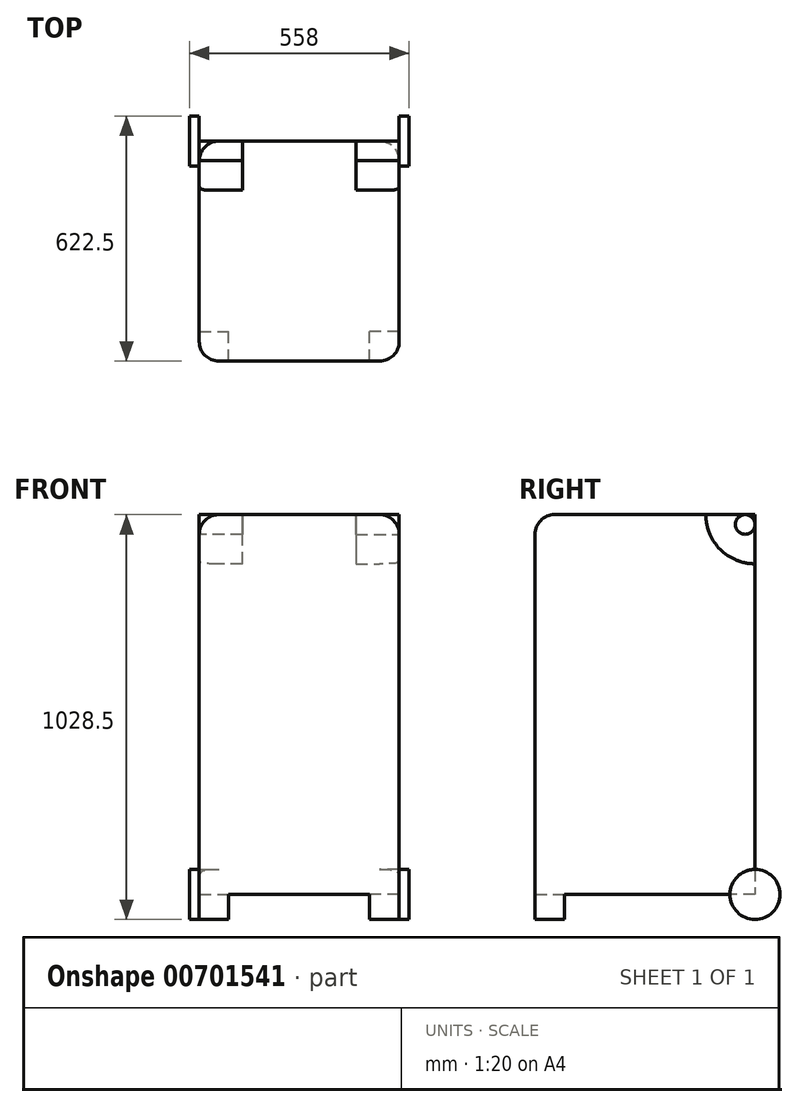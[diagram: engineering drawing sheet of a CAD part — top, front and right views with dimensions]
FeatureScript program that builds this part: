
annotation { "Feature Type Name" : "Feature", "Feature Type Description" : "" }
export const myFeature = defineFeature(function(context is Context, id is Id, definition is map)
    precondition{}
    {
        {
            var Q0;
            Q0=qCreatedBy(makeId("Top.planeOp"),FACE);
            var sketch = newSketch(context, id + "F0", { "sketchPlane" : qUnion([Q0])});
            skLineSegment(sketch, "E0.bottom", {"start": v(-254, 279.5) * mm, "end": v(254, 279.5) * mm});
            skLineSegment(sketch, "E0.top", {"start": v(-254, -279.5) * mm, "end": v(254, -279.5) * mm});
            skLineSegment(sketch, "E0.left", {"start": v(-254, 279.5) * mm, "end": v(-254, -279.5) * mm});
            skLineSegment(sketch, "E0.right", {"start": v(254, 279.5) * mm, "end": v(254, -279.5) * mm});
            skPoint(sketch, "E0.middle", {"position": v(0, 0) * mm});
            skSolve(sketch);
        }
        {
            var Q0;
            Q0=makeQuery(id+"F0.imprint","IMPRINT",FACE,{"disambiguationData":[TD([[makeQuery(id+"F0.imprint","IMPRINT",EDGE,{"derivedFrom":sQuery(id+"F0.wireOp",EDGE,"E0.bottom")}),-1.0]])]});
            extrude(context, id + "F1", {"entities" : qUnion([Q0]), "depth" : 965 * mm, "offsetDistance" : 25 * mm});
        }
        {
            var Q0;
            Q0=makeQuery(id+"F1.opExtrude","SWEPT_FACE",FACE,{"disambiguationData":[OSD([sQuery(id+"F0.wireOp",EDGE,"E0.right")])]});
            var sketch = newSketch(context, id + "F2", { "sketchPlane" : qUnion([Q0])});
            skCircle(sketch, "E1", {"center": v(279.5, 0) * mm, "radius": 63.5 * mm});
            skSolve(sketch);
        }
        {
            var Q0;
            Q0 = qSketchRegion(id + "F2", true);
            extrude(context, id + "F3", {"entities" : qUnion([Q0]), "operationType" : NewBodyOperationType.ADD, "depth" : 25 * mm, "offsetDistance" : 25 * mm});
        }
        {
            var Q0;
            Q0=makeQuery(id+"F1.opExtrude","SWEPT_FACE",FACE,{"disambiguationData":[OSD([sQuery(id+"F0.wireOp",EDGE,"E0.left")])]});
            var sketch = newSketch(context, id + "F4", { "sketchPlane" : qUnion([Q0])});
            skCircle(sketch, "E2", {"center": v(-279.5, 0) * mm, "radius": 63.5 * mm});
            skSolve(sketch);
        }
        {
            var Q0;
            Q0 = qSketchRegion(id + "F4", true);
            extrude(context, id + "F5", {"entities" : qUnion([Q0]), "operationType" : NewBodyOperationType.ADD, "depth" : 25 * mm, "offsetDistance" : 25 * mm});
        }
        {
            var Q0;
            Q0=makeQuery(id+"F1.opExtrude","CAP_FACE",FACE,{"disambiguationData":[OSD([sQuery(id+"F0.wireOp",EDGE,"E0.bottom"),sQuery(id+"F0.wireOp",EDGE,"E0.top"),sQuery(id+"F0.wireOp",EDGE,"E0.left"),sQuery(id+"F0.wireOp",EDGE,"E0.right")])],"isStart":true});
            var sketch = newSketch(context, id + "F6", { "sketchPlane" : qUnion([Q0])});
            skLineSegment(sketch, "E3.bottom", {"start": v(-254, 279.5) * mm, "end": v(-179, 279.5) * mm});
            skLineSegment(sketch, "E3.top", {"start": v(-254, 204.5) * mm, "end": v(-179, 204.5) * mm});
            skLineSegment(sketch, "E3.left", {"start": v(-254, 279.5) * mm, "end": v(-254, 204.5) * mm});
            skLineSegment(sketch, "E3.right", {"start": v(-179, 279.5) * mm, "end": v(-179, 204.5) * mm});
            skLineSegment(sketch, "E4.bottom", {"start": v(254, 279.5) * mm, "end": v(179, 279.5) * mm});
            skLineSegment(sketch, "E4.top", {"start": v(254, 204.5) * mm, "end": v(179, 204.5) * mm});
            skLineSegment(sketch, "E4.left", {"start": v(254, 279.5) * mm, "end": v(254, 204.5) * mm});
            skLineSegment(sketch, "E4.right", {"start": v(179, 279.5) * mm, "end": v(179, 204.5) * mm});
            skSolve(sketch);
        }
        {
            var Q0;
            Q0 = qSketchRegion(id + "F6", true);
            extrude(context, id + "F7", {"entities" : qUnion([Q0]), "operationType" : NewBodyOperationType.ADD, "depth" : 63.5 * mm, "offsetDistance" : 25 * mm});
        }
        {
            var Q0;
            Q0=makeQuery(id+"F7.boolean.opBoolean","MERGE",FACE,{"derivedFrom":[makeQuery(id+"F1.opExtrude","SWEPT_FACE",FACE,{"disambiguationData":[OSD([sQuery(id+"F0.wireOp",EDGE,"E0.left")])]}),makeQuery(id+"F7.opExtrude","SWEPT_FACE",FACE,{"disambiguationData":[OSD([sQuery(id+"F6.wireOp",EDGE,"E3.left")])]})]});
            var sketch = newSketch(context, id + "F8", { "sketchPlane" : qUnion([Q0])});
            skCircle(sketch, "E5", {"center": v(-279.5, 965) * mm, "radius": 125 * mm});
            skCircle(sketch, "E6", {"center": v(-254.5, 940) * mm, "radius": 25 * mm});
            skSolve(sketch);
        }
        {
            var Q0;
            Q0 = qSketchRegion(id + "F8", true);
            extrude(context, id + "F9", {"entities" : qUnion([Q0]), "operationType" : NewBodyOperationType.REMOVE, "oppositeDirection" : true, "depth" : 110 * mm, "offsetDistance" : 25 * mm});
        }
        {
            var Q0;
            Q0=makeQuery(id+"F7.boolean.opBoolean","MERGE",FACE,{"derivedFrom":[makeQuery(id+"F1.opExtrude","SWEPT_FACE",FACE,{"disambiguationData":[OSD([sQuery(id+"F0.wireOp",EDGE,"E0.right")])]}),makeQuery(id+"F7.opExtrude","SWEPT_FACE",FACE,{"disambiguationData":[OSD([sQuery(id+"F6.wireOp",EDGE,"E4.left")])]})]});
            var sketch = newSketch(context, id + "F10", { "sketchPlane" : qUnion([Q0])});
            skCircle(sketch, "E7", {"center": v(279.5, 965) * mm, "radius": 125 * mm});
            skCircle(sketch, "E8", {"center": v(254.5, 940) * mm, "radius": 25 * mm});
            skSolve(sketch);
        }
        {
            var Q0;
            {var subQ1=sQuery(id+"F0.wireOp",EDGE,"E0.right");var subQ3=makeQuery(id+"F1.opExtrude","CAP_EDGE",EDGE,{"disambiguationData":[OSD([subQ1])],"isStart":false});var subQ8=sQuery(id+"F10.wireOp",EDGE,"E7");var subQ9=makeQuery(id+"F10.imprint","INTERSECT",VERTEX,{"derivedFrom":[subQ3,subQ8]});Q0=makeQuery(id+"F10.imprint","IMPRINT",FACE,{"disambiguationData":[TD([[makeQuery(id+"F10.imprint","IMPRINT",EDGE,{"disambiguationData":[TD([[subQ9,1.0]])],"derivedFrom":subQ3}),-1.0]])]});}
            var Q1;
            {var subQ0=sQuery(id+"F10.wireOp",EDGE,"E7");var subQ1=sQuery(id+"F0.wireOp",EDGE,"E0.right");var subQ2=makeQuery(id+"F1.opExtrude","CAP_EDGE",EDGE,{"disambiguationData":[OSD([subQ1])],"isStart":false});var subQ3=makeQuery(id+"F10.imprint","INTERSECT",VERTEX,{"derivedFrom":[subQ2,subQ0]});Q1=makeQuery(id+"F10.imprint","IMPRINT",FACE,{"disambiguationData":[TD([[makeQuery(id+"F10.imprint","IMPRINT",EDGE,{"disambiguationData":[TD([[subQ3,1.0]])],"derivedFrom":subQ2}),1.0]])]});}
            var Q2;
            {var subQ0=sQuery(id+"F10.wireOp",EDGE,"E8");var subQ1=sQuery(id+"F0.wireOp",EDGE,"E0.right");var subQ2=makeQuery(id+"F1.opExtrude","CAP_EDGE",EDGE,{"disambiguationData":[OSD([subQ1])],"isStart":false});var subQ3=makeQuery(id+"F10.imprint","INTERSECT",VERTEX,{"derivedFrom":[subQ2,subQ0]});Q2=makeQuery(id+"F10.imprint","IMPRINT",FACE,{"disambiguationData":[TD([[makeQuery(id+"F10.imprint","IMPRINT",EDGE,{"disambiguationData":[TD([[subQ3,1.0]])],"derivedFrom":subQ0}),-1.0]])]});}
            extrude(context, id + "F11", {"entities" : qUnion([Q0, Q1, Q2]), "operationType" : NewBodyOperationType.REMOVE, "oppositeDirection" : true, "depth" : 110 * mm, "offsetDistance" : 25 * mm});
        }
        {
            var Q0;
            Q0=makeQuery(id+"F7.boolean.opBoolean","MERGE",EDGE,{"derivedFrom":[makeQuery(id+"F1.opExtrude","SWEPT_EDGE",EDGE,{"disambiguationData":[OSD([sQuery(id+"F0.wireOp",EDGE,"E0.top"),sQuery(id+"F0.wireOp",EDGE,"E0.right")])]}),makeQuery(id+"F7.opExtrude","SWEPT_EDGE",EDGE,{"disambiguationData":[OSD([sQuery(id+"F6.wireOp",EDGE,"E4.bottom"),sQuery(id+"F6.wireOp",EDGE,"E4.left")])]})]});
            var Q1;
            Q1=makeQuery(id+"F1.opExtrude","CAP_EDGE",EDGE,{"disambiguationData":[OSD([sQuery(id+"F0.wireOp",EDGE,"E0.right")])],"isStart":false});
            var Q2;
            Q2=makeQuery(id+"F1.opExtrude","CAP_EDGE",EDGE,{"disambiguationData":[OSD([sQuery(id+"F0.wireOp",EDGE,"E0.top")])],"isStart":false});
            var Q3;
            Q3=makeQuery(id+"F7.boolean.opBoolean","MERGE",EDGE,{"derivedFrom":[makeQuery(id+"F1.opExtrude","SWEPT_EDGE",EDGE,{"disambiguationData":[OSD([sQuery(id+"F0.wireOp",EDGE,"E0.top"),sQuery(id+"F0.wireOp",EDGE,"E0.left")])]}),makeQuery(id+"F7.opExtrude","SWEPT_EDGE",EDGE,{"disambiguationData":[OSD([sQuery(id+"F6.wireOp",EDGE,"E3.bottom"),sQuery(id+"F6.wireOp",EDGE,"E3.left")])]})]});
            var Q4;
            Q4=makeQuery(id+"F1.opExtrude","CAP_EDGE",EDGE,{"disambiguationData":[OSD([sQuery(id+"F0.wireOp",EDGE,"E0.left")])],"isStart":false});
            var Q5;
            {var subQ0=sQuery(id+"F0.wireOp",EDGE,"E0.bottom");var subQ1=sQuery(id+"F0.wireOp",EDGE,"E0.right");Q5=makeQuery(id+"F3.boolean.opBoolean","SPLIT",EDGE,{"disambiguationData":[topologyDisambiguationEdgeConnected([makeQuery(id+"F1.opExtrude","SWEPT_FACE",FACE,{"disambiguationData":[OSD([subQ1])]})])],"derivedFrom":makeQuery(id+"F1.opExtrude","SWEPT_EDGE",EDGE,{"disambiguationData":[OSD([subQ0,subQ1])]})});}
            var Q6;
            {var subQ0=sQuery(id+"F0.wireOp",EDGE,"E0.bottom");var subQ1=sQuery(id+"F0.wireOp",EDGE,"E0.left");Q6=makeQuery(id+"F5.boolean.opBoolean","SPLIT",EDGE,{"disambiguationData":[topologyDisambiguationEdgeConnected([makeQuery(id+"F1.opExtrude","SWEPT_FACE",FACE,{"disambiguationData":[OSD([subQ1])]})])],"derivedFrom":makeQuery(id+"F1.opExtrude","SWEPT_EDGE",EDGE,{"disambiguationData":[OSD([subQ0,subQ1])]})});}
            fillet(context, id + "F12", {"entities" : qUnion([Q0, Q1, Q2, Q3, Q4, Q5, Q6]), "radius" : 50 * mm, "tangentPropagation" : true, "allowEdgeOverflow" : false});
        }
    });
